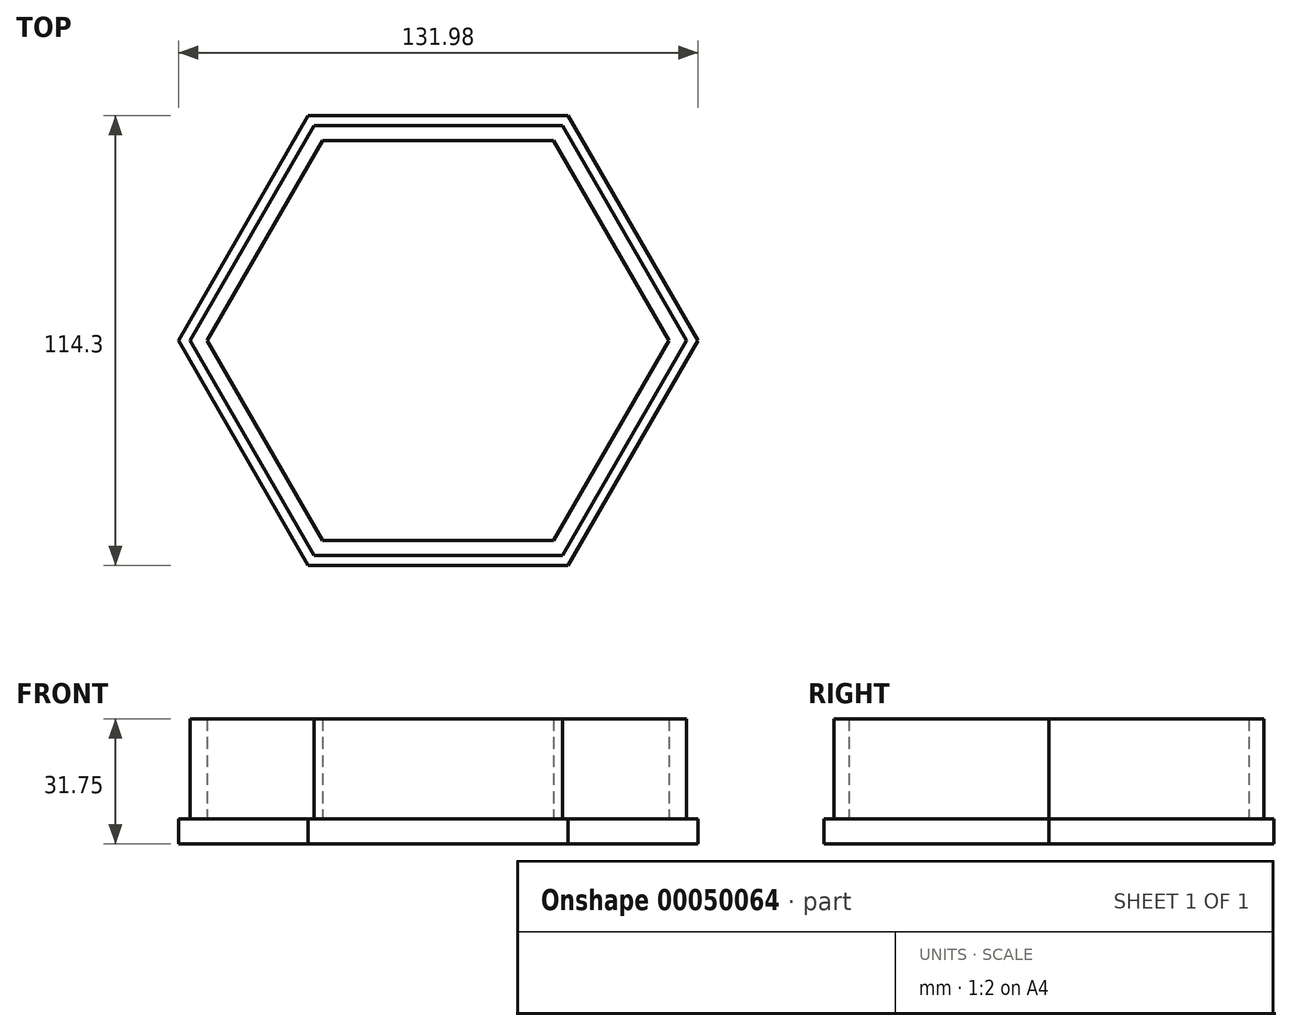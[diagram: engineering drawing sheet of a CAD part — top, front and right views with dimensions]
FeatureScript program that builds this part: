
annotation { "Feature Type Name" : "Feature", "Feature Type Description" : "" }
export const myFeature = defineFeature(function(context is Context, id is Id, definition is map)
    precondition{}
    {
        {
            var Q0;
            Q0=qCreatedBy(makeId("Top.planeOp"),FACE);
            var sketch = newSketch(context, id + "F0", { "sketchPlane" : qUnion([Q0])});
            skCircle(sketch, "E0.cCircle", {"center": v(0, 0) * mm, "radius": 66 * mm, "construction": true});
            skLineSegment(sketch, "E0.0", {"start": v(66, 0) * mm, "end": v(33, -57.15) * mm});
            skLineSegment(sketch, "E0.1", {"start": v(33, -57.15) * mm, "end": v(-33, -57.15) * mm});
            skLineSegment(sketch, "E0.2", {"start": v(-33, -57.15) * mm, "end": v(-66, 0) * mm});
            skLineSegment(sketch, "E0.3", {"start": v(-66, 0) * mm, "end": v(-33, 57.15) * mm});
            skLineSegment(sketch, "E0.4", {"start": v(-33, 57.15) * mm, "end": v(33, 57.15) * mm});
            skLineSegment(sketch, "E0.5", {"start": v(33, 57.15) * mm, "end": v(66, 0) * mm});
            skSolve(sketch);
        }
        {
            var Q0;
            Q0=makeQuery(id+"F0.imprint","IMPRINT",FACE,{"disambiguationData":[TD([[makeQuery(id+"F0.imprint","IMPRINT",EDGE,{"derivedFrom":sQuery(id+"F0.wireOp",EDGE,"E0.0")}),-1.0]])]});
            extrude(context, id + "F1", {"entities" : qUnion([Q0]), "oppositeDirection" : true, "depth" : 6.35 * mm});
        }
        {
            var Q0;
            Q0=qCreatedBy(makeId("Top.planeOp"),FACE);
            var sketch = newSketch(context, id + "F2", { "sketchPlane" : qUnion([Q0])});
            skCircle(sketch, "E1.cCircle", {"center": v(0, 0) * mm, "radius": 58.66 * mm, "construction": true});
            skLineSegment(sketch, "E1.0", {"start": v(58.66, 0) * mm, "end": v(29.33, -50.8) * mm});
            skLineSegment(sketch, "E1.1", {"start": v(29.33, -50.8) * mm, "end": v(-29.33, -50.8) * mm});
            skLineSegment(sketch, "E1.2", {"start": v(-29.33, -50.8) * mm, "end": v(-58.66, 0) * mm});
            skLineSegment(sketch, "E1.3", {"start": v(-58.66, 0) * mm, "end": v(-29.33, 50.8) * mm});
            skLineSegment(sketch, "E1.4", {"start": v(-29.33, 50.8) * mm, "end": v(29.33, 50.8) * mm});
            skLineSegment(sketch, "E1.5", {"start": v(29.33, 50.8) * mm, "end": v(58.66, 0) * mm});
            skCircle(sketch, "E2.cCircle", {"center": v(0, 0) * mm, "radius": 54.61 * mm, "construction": true});
            skLineSegment(sketch, "E2.0", {"start": v(63.06, 0) * mm, "end": v(31.53, -54.61) * mm});
            skLineSegment(sketch, "E2.1", {"start": v(31.53, -54.6) * mm, "end": v(-31.53, -54.61) * mm});
            skLineSegment(sketch, "E2.2", {"start": v(-31.53, -54.61) * mm, "end": v(-63.06, 0) * mm});
            skLineSegment(sketch, "E2.3", {"start": v(-63.06, 0) * mm, "end": v(-31.53, 54.61) * mm});
            skLineSegment(sketch, "E2.4", {"start": v(-31.53, 54.61) * mm, "end": v(31.53, 54.61) * mm});
            skLineSegment(sketch, "E2.5", {"start": v(31.53, 54.6) * mm, "end": v(63.06, 0) * mm});
            skPoint(sketch, "E2.0.midPoint", {"position": v(47.3, -27.3) * mm});
            skSolve(sketch);
        }
        {
            var Q0;
            Q0 = qSketchRegion(id + "F2", true);
            extrude(context, id + "F3", {"entities" : qUnion([Q0]), "operationType" : NewBodyOperationType.ADD, "depth" : 25.4 * mm});
        }
    });
